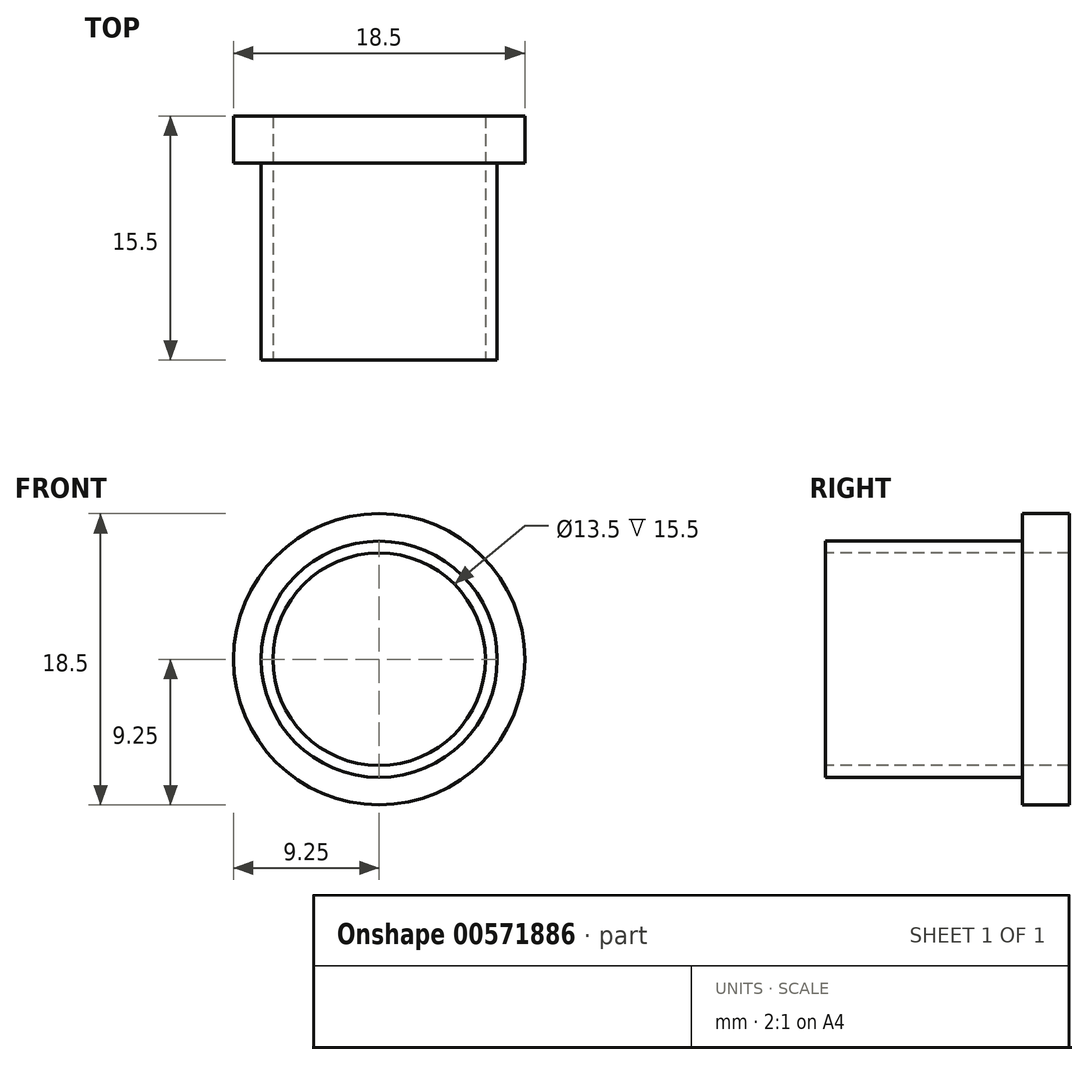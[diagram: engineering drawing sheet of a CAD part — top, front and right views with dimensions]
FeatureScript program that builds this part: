
annotation { "Feature Type Name" : "Feature", "Feature Type Description" : "" }
export const myFeature = defineFeature(function(context is Context, id is Id, definition is map)
    precondition{}
    {
        {
            var Q0;
            Q0=qCreatedBy(makeId("Top.planeOp"),FACE);
            var sketch = newSketch(context, id + "F0", { "sketchPlane" : qUnion([Q0])});
            skLineSegment(sketch, "E0", {"start": v(0, 0) * mm, "end": v(7.5, 0) * mm});
            skLineSegment(sketch, "E1", {"start": v(7.5, 0) * mm, "end": v(7.5, -12.5) * mm});
            skLineSegment(sketch, "E2", {"start": v(7.5, -12.5) * mm, "end": v(0, -12.5) * mm});
            skLineSegment(sketch, "E3", {"start": v(0, -12.5) * mm, "end": v(0, 0) * mm});
            skLineSegment(sketch, "E4", {"start": v(7.5, 0) * mm, "end": v(9.25, 0) * mm});
            skLineSegment(sketch, "E5", {"start": v(9.25, 0) * mm, "end": v(9.25, 3) * mm});
            skLineSegment(sketch, "E6", {"start": v(9.25, 3) * mm, "end": v(0, 3) * mm});
            skLineSegment(sketch, "E7", {"start": v(0, 3) * mm, "end": v(0, 0) * mm});
            skLineSegment(sketch, "E8", {"start": v(0, -12.5) * mm, "end": v(6.75, -12.5) * mm});
            skLineSegment(sketch, "E9", {"start": v(6.75, -12.5) * mm, "end": v(6.75, 3) * mm});
            skSolve(sketch);
        }
        {
            var Q0;
            {var subQ4=sQuery(id+"F0.wireOp",EDGE,"E4");Q0=makeQuery(id+"F0.imprint","IMPRINT",FACE,{"disambiguationData":[TD([[makeQuery(id+"F0.imprint","IMPRINT",EDGE,{"derivedFrom":subQ4}),1.0]])]});}
            var Q1;
            {var subQ0=sQuery(id+"F0.wireOp",EDGE,"E1");Q1=makeQuery(id+"F0.imprint","IMPRINT",FACE,{"disambiguationData":[TD([[makeQuery(id+"F0.imprint","IMPRINT",EDGE,{"derivedFrom":subQ0}),-1.0]])]});}
            var Q2;
            Q2=sQuery(id+"F0.wireOp",EDGE,"E3");
            revolve(context, id + "F1", {"entities" : qUnion([Q0, Q1]), "axis" : qUnion([Q2]), "revolveType" : RevolveType.FULL});
        }
    });
